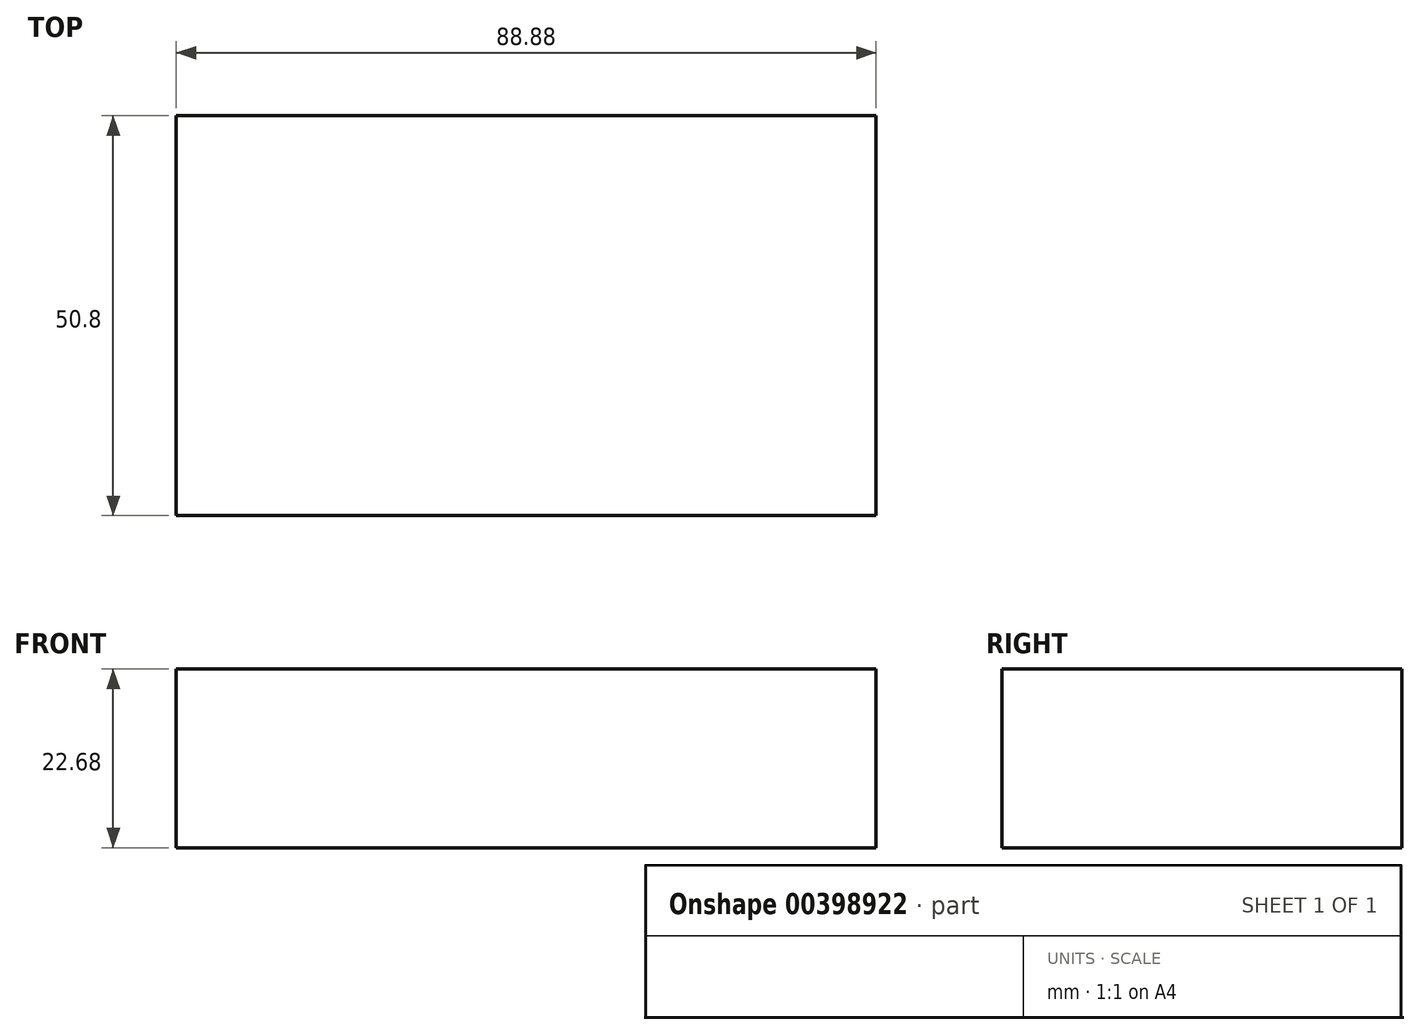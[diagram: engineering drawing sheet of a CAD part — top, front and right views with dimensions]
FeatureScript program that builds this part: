
annotation { "Feature Type Name" : "Feature", "Feature Type Description" : "" }
export const myFeature = defineFeature(function(context is Context, id is Id, definition is map)
    precondition{}
    {
        {
            var Q0;
            Q0=qCreatedBy(makeId("Front.planeOp"),FACE);
            var sketch = newSketch(context, id + "F0", { "sketchPlane" : qUnion([Q0])});
            skLineSegment(sketch, "E0.bottom", {"start": v(44.44, -11.34) * mm, "end": v(-44.44, -11.34) * mm});
            skLineSegment(sketch, "E0.top", {"start": v(44.44, 11.34) * mm, "end": v(-44.44, 11.34) * mm});
            skLineSegment(sketch, "E0.left", {"start": v(44.44, -11.34) * mm, "end": v(44.44, 11.34) * mm});
            skLineSegment(sketch, "E0.right", {"start": v(-44.44, -11.34) * mm, "end": v(-44.44, 11.34) * mm});
            skPoint(sketch, "E0.middle", {"position": v(0, 0) * mm});
            skSolve(sketch);
        }
        {
            var Q0;
            Q0 = qSketchRegion(id + "F0", true);
            extrude(context, id + "F1", {"entities" : qUnion([Q0]), "depth" : 25.4 * mm, "hasSecondDirection" : true, "secondDirectionOppositeDirection" : true, "secondDirectionDepth" : 25.4 * mm});
        }
    });
